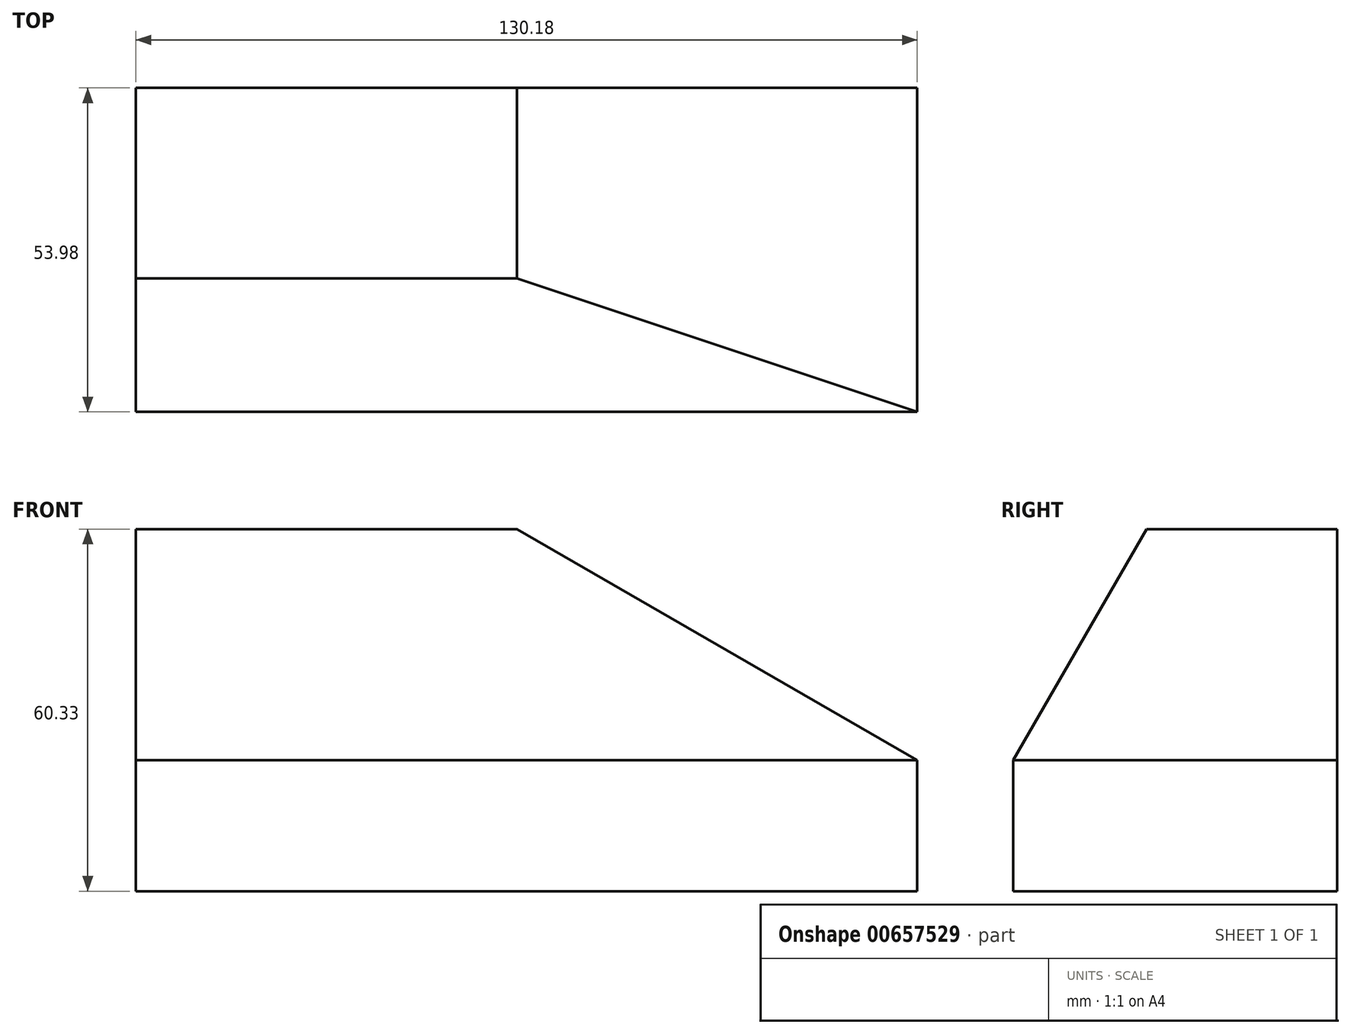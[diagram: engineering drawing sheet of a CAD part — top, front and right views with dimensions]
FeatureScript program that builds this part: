
annotation { "Feature Type Name" : "Feature", "Feature Type Description" : "" }
export const myFeature = defineFeature(function(context is Context, id is Id, definition is map)
    precondition{}
    {
        {
            var Q0;
            Q0=qCreatedBy(makeId("Front.planeOp"),FACE);
            var sketch = newSketch(context, id + "F0", { "sketchPlane" : qUnion([Q0])});
            skLineSegment(sketch, "E0", {"start": v(0, 0) * mm, "end": v(-130.18, 0) * mm});
            skLineSegment(sketch, "E1", {"start": v(-130.18, 0) * mm, "end": v(-130.18, 60.32) * mm});
            skLineSegment(sketch, "E2", {"start": v(-130.18, 60.32) * mm, "end": v(-66.68, 60.32) * mm});
            skLineSegment(sketch, "E3", {"start": v(-66.68, 60.33) * mm, "end": v(-5.57, 25.05) * mm});
            skLineSegment(sketch, "E4", {"start": v(-66.68, 60.32) * mm, "end": v(0, 21.83) * mm});
            skLineSegment(sketch, "E5", {"start": v(0, 21.83) * mm, "end": v(0, 0) * mm});
            skSolve(sketch);
        }
        {
            var Q0;
            Q0=makeQuery(id+"F0.imprint","IMPRINT",FACE,{"disambiguationData":[TD([[makeQuery(id+"F0.imprint","IMPRINT",EDGE,{"derivedFrom":sQuery(id+"F0.wireOp",EDGE,"E0")}),-1.0]])]});
            extrude(context, id + "F1", {"entities" : qUnion([Q0]), "depth" : 53.97 * mm, "offsetDistance" : 25.4 * mm});
        }
        {
            var Q0;
            Q0=makeQuery(id+"F1.opExtrude","SWEPT_FACE",FACE,{"disambiguationData":[OSD([sQuery(id+"F0.wireOp",EDGE,"E1")])]});
            var sketch = newSketch(context, id + "F2", { "sketchPlane" : qUnion([Q0])});
            skLineSegment(sketch, "E6", {"start": v(53.98, 21.82) * mm, "end": v(31.74, 60.32) * mm});
            skLineSegment(sketch, "E7", {"start": v(31.74, 60.32) * mm, "end": v(53.98, 60.32) * mm});
            skSolve(sketch);
        }
        {
            var Q0;
            {var subQ0=sQuery(id+"F2.wireOp",EDGE,"E6");Q0=makeQuery(id+"F2.imprint","IMPRINT",FACE,{"disambiguationData":[TD([[makeQuery(id+"F2.imprint","IMPRINT",EDGE,{"derivedFrom":subQ0}),-1.0]])]});}
            extrude(context, id + "F3", {"entities" : qUnion([Q0]), "operationType" : NewBodyOperationType.REMOVE, "endBound" : BoundingType.UP_TO_NEXT, "oppositeDirection" : true, "depth" : 130.17 * mm, "offsetDistance" : 25.4 * mm});
        }
    });
